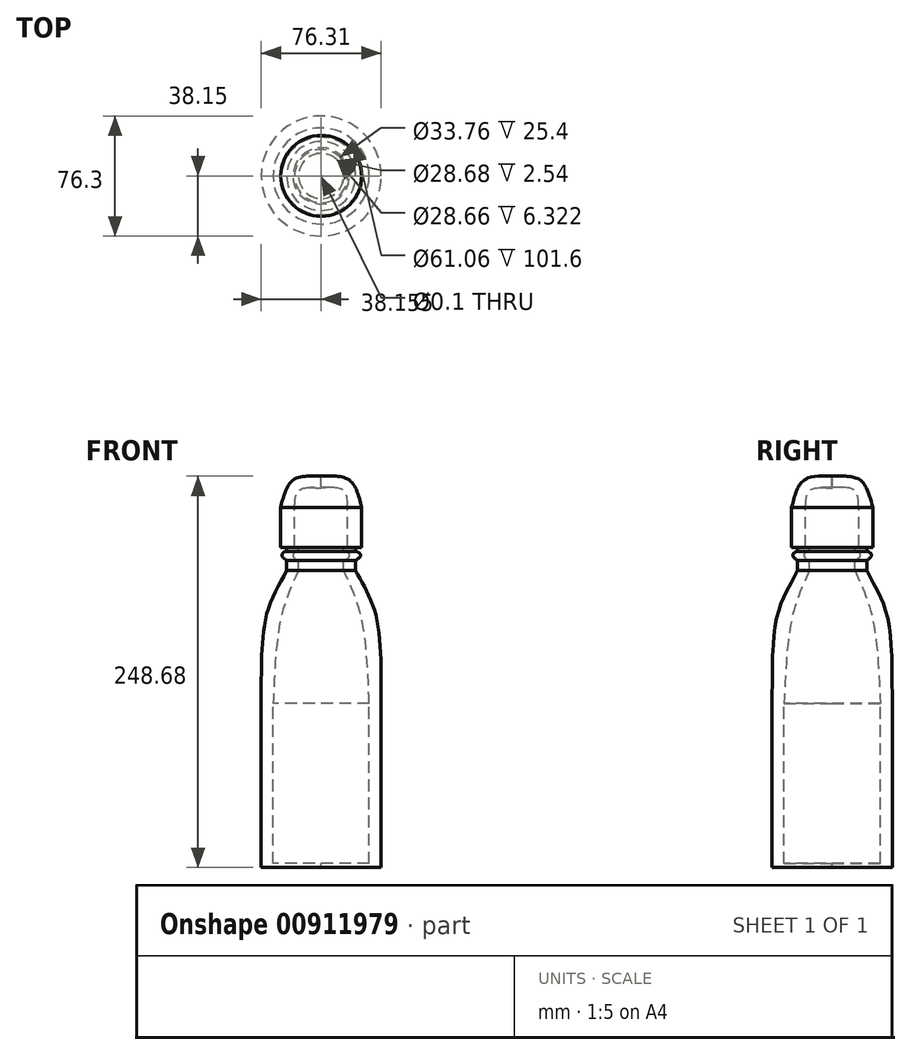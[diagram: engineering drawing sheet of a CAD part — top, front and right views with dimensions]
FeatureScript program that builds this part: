
annotation { "Feature Type Name" : "Feature", "Feature Type Description" : "" }
export const myFeature = defineFeature(function(context is Context, id is Id, definition is map)
    precondition{}
    {
        {
            var Q0;
            Q0=qCreatedBy(makeId("Front.planeOp"),FACE);
            var sketch = newSketch(context, id + "F0", { "sketchPlane" : qUnion([Q0])});
            skLineSegment(sketch, "E0.top", {"start": v(-19.13, 0) * mm, "end": v(-26.75, 0) * mm});
            skLineSegment(sketch, "E0.left", {"start": v(-19.13, 101.6) * mm, "end": v(-19.13, 0) * mm});
            skLineSegment(sketch, "E0.right", {"start": v(-26.75, 101.6) * mm, "end": v(-26.75, 0) * mm});
            skLineSegment(sketch, "E1", {"start": v(-57.29, 101.61) * mm, "end": v(-57.29, 0) * mm, "construction": true});
            skLineSegment(sketch, "E2.bottom", {"start": v(-19.13, 0) * mm, "end": v(-57.23, 0) * mm});
            skLineSegment(sketch, "E2.top", {"start": v(-19.13, -2.54) * mm, "end": v(-57.23, -2.54) * mm});
            skLineSegment(sketch, "E2.left", {"start": v(-19.13, 0) * mm, "end": v(-19.13, -2.54) * mm});
            skLineSegment(sketch, "E2.right", {"start": v(-57.23, 0) * mm, "end": v(-57.23, -2.54) * mm});
            skLineSegment(sketch, "E3", {"start": v(-57.29, 101.61) * mm, "end": v(-26.75, 101.6) * mm, "construction": true});
            skLineSegment(sketch, "E4", {"start": v(-26.75, 101.6) * mm, "end": v(-19.13, 101.6) * mm});
            skFitSpline(sketch, "E5", {"points": [v(-19.13, 101.6) * mm, v(-22.87, 159.1) * mm, v(-35.34, 186.25) * mm], "startDerivative": vector(-1.07, 107.91) * mm, "endDerivative": vector(-28.35, 58.58) * mm});
            skFitSpline(sketch, "E6", {"points": [v(-26.75, 101.6) * mm, v(-31.86, 156.56) * mm, v(-42.96, 186.28) * mm], "startDerivative": vector(-4.24, 104.48) * mm, "endDerivative": vector(-29.22, 62.97) * mm});
            skLineSegment(sketch, "E7", {"start": v(-42.96, 186.28) * mm, "end": v(-35.34, 186.25) * mm});
            skLineSegment(sketch, "E8", {"start": v(-42.96, 186.28) * mm, "end": v(-42.96, 192.6) * mm});
            skLineSegment(sketch, "E9", {"start": v(-35.34, 186.25) * mm, "end": v(-35.34, 192.6) * mm});
            skLineSegment(sketch, "E10", {"start": v(-42.96, 192.6) * mm, "end": v(-35.34, 192.6) * mm});
            skLineSegment(sketch, "E11", {"start": v(-57.29, 101.61) * mm, "end": v(-57.23, 259.22) * mm, "construction": true});
            skFitSpline(sketch, "E12", {"points": [v(-35.34, 192.6) * mm, v(-32.28, 196.11) * mm, v(-35.34, 198.35) * mm], "startDerivative": vector(14.4, 9.63) * mm, "endDerivative": vector(-13.62, 3.64) * mm});
            skLineSegment(sketch, "E13", {"start": v(-35.34, 198.35) * mm, "end": v(-35.34, 200.89) * mm});
            skLineSegment(sketch, "E14", {"start": v(-31.53, 200.89) * mm, "end": v(-35.34, 200.89) * mm});
            skFitSpline(sketch, "E15", {"points": [v(-42.92, 192.6) * mm, v(-39.33, 196.1) * mm, v(-42.95, 198.7) * mm], "startDerivative": vector(18.23, 8.59) * mm, "endDerivative": vector(-17.11, 5.43) * mm});
            skLineSegment(sketch, "E16", {"start": v(-42.95, 198.7) * mm, "end": v(-42.95, 201.24) * mm});
            skLineSegment(sketch, "E17", {"start": v(-31.53, 200.89) * mm, "end": v(-31.53, 226.29) * mm});
            skLineSegment(sketch, "E18", {"start": v(-42.95, 201.24) * mm, "end": v(-40.4, 201.24) * mm});
            skLineSegment(sketch, "E19", {"start": v(-40.4, 201.24) * mm, "end": v(-40.4, 226.64) * mm});
            skFitSpline(sketch, "E20", {"points": [v(-31.53, 226.29) * mm, v(-38.7, 243) * mm, v(-57.23, 245.98) * mm], "startDerivative": vector(-9.89, 37.31) * mm, "endDerivative": vector(-48.74, -1.82) * mm});
            skFitSpline(sketch, "E21", {"points": [v(-40.4, 226.64) * mm, v(-42.86, 236.89) * mm, v(-57.23, 238.55) * mm], "startDerivative": vector(-1.69, 21.26) * mm, "endDerivative": vector(-30.65, -1.4) * mm});
            skLineSegment(sketch, "E22", {"start": v(-57.23, 245.98) * mm, "end": v(-57.23, 238.55) * mm});
            skSolve(sketch);
        }
        {
            var Q0;
            {var subQ0=sQuery(id+"F0.wireOp",EDGE,"E12");var subQ7=makeQuery(id+"F0.imprint","IMPRINT",EDGE,{"derivedFrom":sQuery(id+"F0.wireOp",EDGE,"E7")});var subQ8=makeQuery(id+"F0.imprint","IMPRINT",EDGE,{"derivedFrom":sQuery(id+"F0.wireOp",EDGE,"E4")});var subQ9=makeQuery(id+"F0.imprint","IMPRINT",EDGE,{"derivedFrom":sQuery(id+"F0.wireOp",EDGE,"E0.top")});Q0=qUnion([makeQuery(id+"F0.imprint","IMPRINT",FACE,{"disambiguationData":[TD([[subQ9,1.0]])]}),makeQuery(id+"F0.imprint","IMPRINT",FACE,{"disambiguationData":[TD([[makeQuery(id+"F0.imprint","IMPRINT",EDGE,{"derivedFrom":subQ0}),1.0]])]}),makeQuery(id+"F0.imprint","IMPRINT",FACE,{"disambiguationData":[TD([[subQ9,-1.0]])]}),makeQuery(id+"F0.imprint","IMPRINT",FACE,{"disambiguationData":[TD([[subQ8,1.0]])]}),makeQuery(id+"F0.imprint","IMPRINT",FACE,{"disambiguationData":[TD([[subQ7,1.0]])]})]);}
            var Q1;
            Q1=sQuery(id+"F0.wireOp",EDGE,"E1");
            revolve(context, id + "F1", {"surfaceOperationType" : NewSurfaceOperationType.NEW, "entities" : qUnion([Q0]), "axis" : qUnion([Q1]), "revolveType" : RevolveType.FULL});
        }
    });
